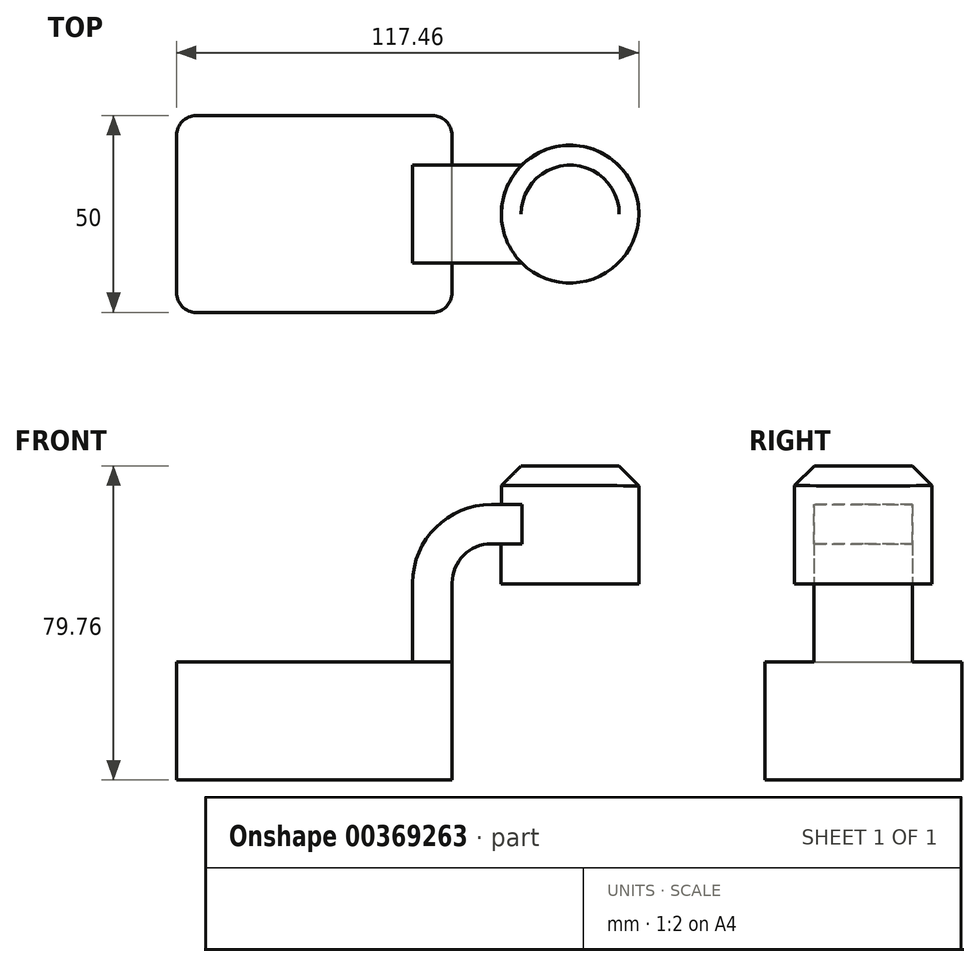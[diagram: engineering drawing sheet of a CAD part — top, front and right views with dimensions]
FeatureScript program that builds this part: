
annotation { "Feature Type Name" : "Feature", "Feature Type Description" : "" }
export const myFeature = defineFeature(function(context is Context, id is Id, definition is map)
    precondition{}
    {
        {
            var Q0;
            Q0=qCreatedBy(makeId("Front.planeOp"),FACE);
            var sketch = newSketch(context, id + "F0", { "sketchPlane" : qUnion([Q0])});
            skLineSegment(sketch, "E0.bottom", {"start": v(-35, 15) * mm, "end": v(35, 15) * mm});
            skLineSegment(sketch, "E0.top", {"start": v(-35, -15) * mm, "end": v(35, -15) * mm});
            skLineSegment(sketch, "E0.left", {"start": v(-35, 15) * mm, "end": v(-35, -15) * mm});
            skLineSegment(sketch, "E0.right", {"start": v(35, 15) * mm, "end": v(35, -15) * mm});
            skPoint(sketch, "E0.middle", {"position": v(0, 0) * mm});
            skLineSegment(sketch, "E1.bottom", {"start": v(82.46, 64.73) * mm, "end": v(47.46, 64.73) * mm});
            skLineSegment(sketch, "E1.top", {"start": v(82.46, 34.73) * mm, "end": v(47.46, 34.73) * mm});
            skLineSegment(sketch, "E1.left", {"start": v(82.46, 64.73) * mm, "end": v(82.46, 34.73) * mm});
            skLineSegment(sketch, "E1.right", {"start": v(47.46, 64.73) * mm, "end": v(47.46, 34.73) * mm});
            skPoint(sketch, "E1.middle", {"position": v(64.96, 49.73) * mm});
            skLineSegment(sketch, "E2", {"start": v(35, 15) * mm, "end": v(35, 35) * mm});
            skArc(sketch, "E3", {"start": v(35, 35) * mm, "mid": v(37.93, 42.07) * mm, "end": v(45, 45) * mm});
            skLineSegment(sketch, "E4", {"start": v(45, 45) * mm, "end": v(65, 45) * mm});
            skLineSegment(sketch, "E5.0", {"start": v(45, 55) * mm, "end": v(65, 55) * mm});
            skArc(sketch, "E5.1", {"start": v(25, 35) * mm, "mid": v(30.86, 49.14) * mm, "end": v(45, 55) * mm});
            skLineSegment(sketch, "E5.2", {"start": v(25, 15) * mm, "end": v(25, 35) * mm});
            skFitSpline(sketch, "E6", {"points": [v(-35, 15) * mm, v(45, 55) * mm], "startDerivative": vector(29.12, 100.73) * mm, "endDerivative": vector(109.13, -2.29) * mm});
            skLineSegment(sketch, "E7", {"start": v(64.96, 34.73) * mm, "end": v(65, 64.73) * mm});
            skSolve(sketch);
        }
        {
            var Q0;
            Q0=makeQuery(id+"F0.imprint","IMPRINT",FACE,{"disambiguationData":[TD([[makeQuery(id+"F0.imprint","IMPRINT",EDGE,{"derivedFrom":sQuery(id+"F0.wireOp",EDGE,"E0.top")}),1.0]])]});
            extrude(context, id + "F1", {"entities" : qUnion([Q0]), "depth" : 50 * mm, "symmetric" : true});
        }
        {
            var Q0;
            Q0=makeQuery(id+"F0.imprint","IMPRINT",FACE,{"disambiguationData":[TD([[makeQuery(id+"F0.imprint","IMPRINT",EDGE,{"derivedFrom":sQuery(id+"F0.wireOp",EDGE,"E5.1")}),1.0]])]});
            extrude(context, id + "F2", {"entities" : qUnion([Q0]), "operationType" : NewBodyOperationType.ADD, "depth" : 15 * mm, "symmetric" : true});
        }
        {
            var Q0;
            {var subQ1=sQuery(id+"F0.wireOp",EDGE,"E2");Q0=makeQuery(id+"F0.imprint","IMPRINT",FACE,{"disambiguationData":[TD([[makeQuery(id+"F0.imprint","IMPRINT",EDGE,{"derivedFrom":subQ1}),1.0]])]});}
            extrude(context, id + "F3", {"entities" : qUnion([Q0]), "operationType" : NewBodyOperationType.ADD, "depth" : 25 * mm, "symmetric" : true});
        }
        {
            var Q0;
            {var subQ0=sQuery(id+"F0.wireOp",EDGE,"E5.0");var subQ1=sQuery(id+"F0.wireOp",EDGE,"E1.right");var subQ2=makeQuery(id+"F0.imprint","INTERSECT",VERTEX,{"derivedFrom":[subQ1,subQ0]});Q0=makeQuery(id+"F0.imprint","IMPRINT",FACE,{"disambiguationData":[TD([[makeQuery(id+"F0.imprint","IMPRINT",EDGE,{"disambiguationData":[TD([[subQ2,-1.0]])],"derivedFrom":subQ1}),1.0]])]});}
            extrude(context, id + "F4", {"entities" : qUnion([Q0]), "operationType" : NewBodyOperationType.ADD, "depth" : 25 * mm, "symmetric" : true});
        }
        {
            var Q0;
            {var subQ0=sQuery(id+"F0.wireOp",EDGE,"E1.left");Q0=makeQuery(id+"F0.imprint","IMPRINT",FACE,{"disambiguationData":[TD([[makeQuery(id+"F0.imprint","IMPRINT",EDGE,{"derivedFrom":subQ0}),-1.0]])]});}
            var Q1;
            Q1=sQuery(id+"F0.wireOp",EDGE,"E7");
            revolve(context, id + "F5", {"operationType" : NewBodyOperationType.ADD, "entities" : qUnion([Q0]), "axis" : qUnion([Q1]), "revolveType" : RevolveType.FULL});
        }
        {
            var Q0;
            Q0=makeQuery(id+"F1.opExtrude","CAP_EDGE",EDGE,{"disambiguationData":[OSD([sQuery(id+"F0.wireOp",EDGE,"E0.right")])],"isStart":false});
            var Q1;
            Q1=makeQuery(id+"F1.opExtrude","CAP_EDGE",EDGE,{"disambiguationData":[OSD([sQuery(id+"F0.wireOp",EDGE,"E0.left")])],"isStart":false});
            var Q2;
            Q2=makeQuery(id+"F1.opExtrude","CAP_EDGE",EDGE,{"disambiguationData":[OSD([sQuery(id+"F0.wireOp",EDGE,"E0.left")])],"isStart":true});
            var Q3;
            Q3=makeQuery(id+"F1.opExtrude","CAP_EDGE",EDGE,{"disambiguationData":[OSD([sQuery(id+"F0.wireOp",EDGE,"E0.right")])],"isStart":true});
            var Q4;
            Q4=makeQuery(id+"F2.opExtrude","CAP_EDGE",EDGE,{"disambiguationData":[OSD([sQuery(id+"F0.wireOp",EDGE,"E6")])],"isStart":false});
            var Q5;
            Q5=makeQuery(id+"F2.opExtrude","CAP_EDGE",EDGE,{"disambiguationData":[OSD([sQuery(id+"F0.wireOp",EDGE,"E6")])],"isStart":true});
            fillet(context, id + "F6", {"entities" : qUnion([Q0, Q1, Q2, Q3, Q4, Q5]), "radius" : 5 * mm, "tangentPropagation" : true, "allowEdgeOverflow" : false});
        }
        {
            var Q0;
            Q0=makeQuery(id+"F5.opRevolve","SWEPT_EDGE",EDGE,{"disambiguationData":[OSD([sQuery(id+"F0.wireOp",EDGE,"E1.bottom"),sQuery(id+"F0.wireOp",EDGE,"E1.left")])]});
            chamfer(context, id + "F7", {"entities" : qUnion([Q0]), "width" : 5 * mm, "tangentPropagation" : true});
        }
    });
